# Revit family: Plum Fix_Basin_Semi Recessed_Argent_Zen 550mm
name_source: partatom
category: Plumbing Fixtures
revit_build: Autodesk Revit 2016 (Build: 20150220_1215(x64)
units: mm (PartAtom-declared; Revit-internal decimal feet)

## family parameters
Always vertical = Yes
Cut with Voids When Loaded = Yes
OmniClass Number = 23.45.05.14.14
OmniClass Title = Sinks/Lavatories
Part Type = Normal
Room Calculation Point = No
Round Connector Dimension = Use Diameter
Shared = No
Work Plane-Based = No

## types (1)
- 1 Tap Hole
    Body Material = z_Argent_Ceramic White
    CW Connection = No
    CWFU = 0
    Cost = 0 $
    Description = Zen 550 Semi Recessed Basin
    HW Connection = No
    HWFU = 0
    Manufacturer = Argent
    Manufacturer_Overall Depth = 430 mm  [stored 1.41076 ft]
    Manufacturer_Overall Height = 216 mm  [stored 0.708661 ft]
    Manufacturer_Overall Width = 550 mm
    Manufacturer_Spec Code = FC11TUL01
    Manufacturer_URL__Product Specific = https://www.argentaust.com.au
    Model = FC11TUL01
    ModifiedIssue_ANZRS = 20190726 $
    Type Comments = 1 Tap Hole
    URL = https://www.argentaust.com.au
    Vent Connection = No
    WFU = 0
    Waste Connection = Yes

note: [stored X ft] marks values corroborated as IEEE doubles in the binary element streams (Revit-internal decimal feet)

## geometry (parser evidence)
native form markers: Sweep x5
no freeform markers — native parametric forms only
